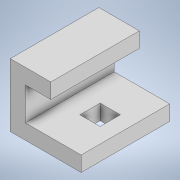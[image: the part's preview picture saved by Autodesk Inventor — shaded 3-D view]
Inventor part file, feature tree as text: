
AUTODESK INVENTOR PART (.ipt)
format: ipt  version: 2022 (Build 260153000, 153)  size: 110,592 bytes
history: native  units: mm
features: extrude x2, sketch x2, other x1
ambient origin geometry x8: Origin, YZ Plane, XZ Plane, XY Plane, X Axis, Y Axis, Z Axis, Center Point
bodies: Body1 (feature_tree)
feature tree (5):
  other  "Sólido1"
  extrude  "Extrusão1"  Depth=50.0mm
  extrude  "Extrusão2"  Depth=12.0mm
  sketch  "Esboço1"  dims[d3=56.0mm d4=50.0mm]
  sketch  "Esboço2"  dims[d5=32.0mm d6=12.0mm d7=70.0mm d8=0.0mm d9=16.0mm d10=16.0mm d11=27.0mm d13=12.0mm d14=0.0mm d15=0.0mm]
